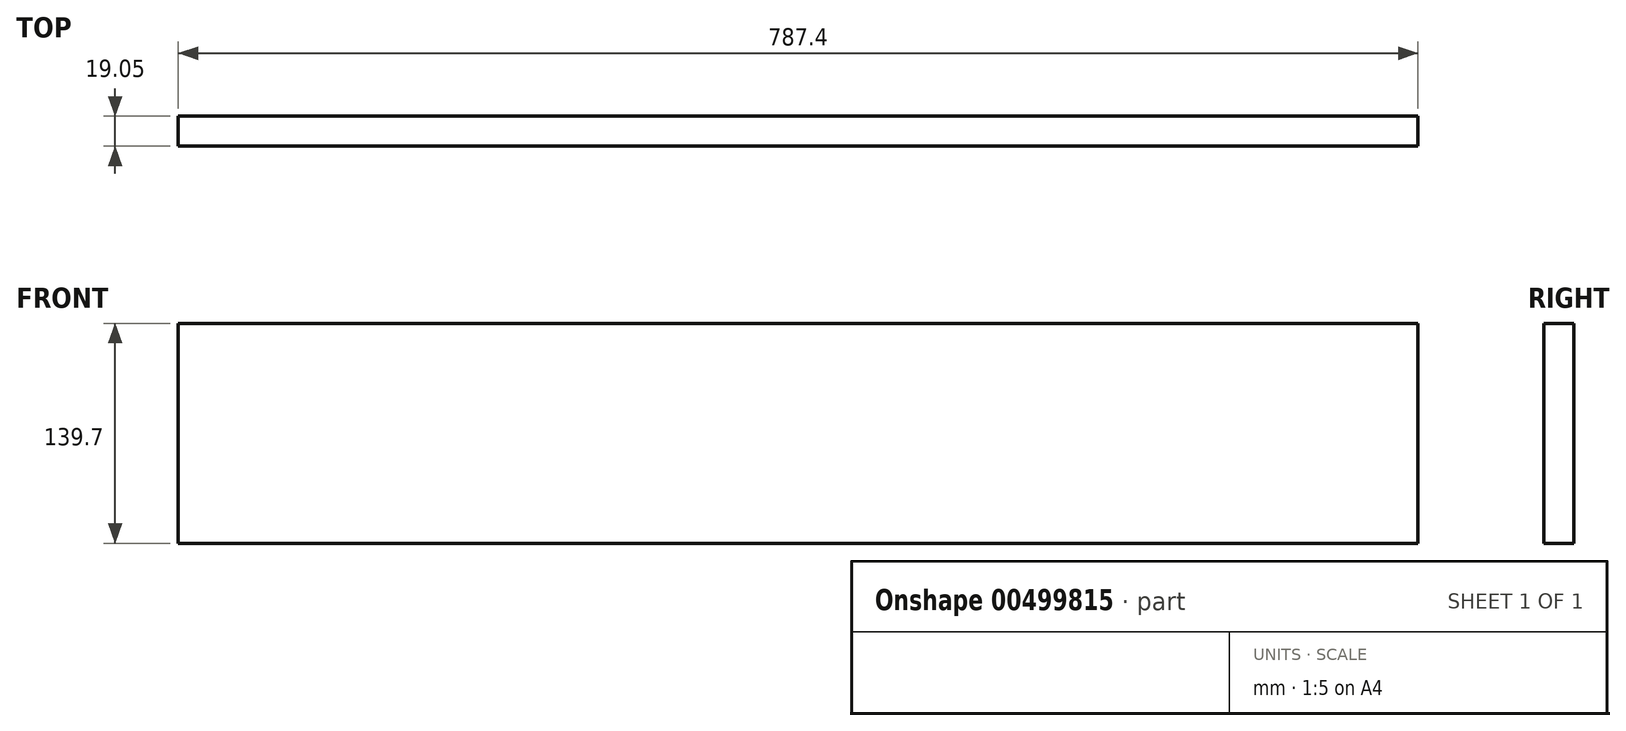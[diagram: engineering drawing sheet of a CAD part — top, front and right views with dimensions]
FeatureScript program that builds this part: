
annotation { "Feature Type Name" : "Feature", "Feature Type Description" : "" }
export const myFeature = defineFeature(function(context is Context, id is Id, definition is map)
    precondition{}
    {
        {
            var Q0;
            Q0=qCreatedBy(makeId("Front.planeOp"),FACE);
            var sketch = newSketch(context, id + "F0", { "sketchPlane" : qUnion([Q0])});
            skLineSegment(sketch, "E0.bottom", {"start": v(393.7, -69.85) * mm, "end": v(-393.7, -69.85) * mm});
            skLineSegment(sketch, "E0.top", {"start": v(393.7, 69.85) * mm, "end": v(-393.7, 69.85) * mm});
            skLineSegment(sketch, "E0.left", {"start": v(393.7, -69.85) * mm, "end": v(393.7, 69.85) * mm});
            skLineSegment(sketch, "E0.right", {"start": v(-393.7, -69.85) * mm, "end": v(-393.7, 69.85) * mm});
            skPoint(sketch, "E0.middle", {"position": v(0, 0) * mm});
            skSolve(sketch);
        }
        {
            var Q0;
            Q0 = qSketchRegion(id + "F0", true);
            extrude(context, id + "F1", {"entities" : qUnion([Q0]), "depth" : 19.05 * mm});
        }
    });
